# Revit family: Bath&ShoverMixer-Joystick-FloorMounted-Vitra-İstanbulSeries-A41819
name_source: partatom
category: Plumbing Fixtures
revit_build: Autodesk Revit 2017 (Build: 20160225_1515(x64)
units: mm (PartAtom-declared; Revit-internal decimal feet)

## family parameters
Cut with Voids When Loaded = No
Host = Face
OmniClass Number = 23.45.55.17
OmniClass Title = Mixing Faucets
Part Type = Normal
Room Calculation Point = No
Round Connector Dimension = Use Diameter
Shared = Yes

## types (7) — shared parameters
BIMobject category = Bath/Shower Mixer
Brand = Vitra
CW Connection = Yes
Description = Istanbul Joystick Bath/Shower Mixer
with Handshower-Floor Mounted
Design country = Turkey
HW Connection = Yes
Hot Water Supply (max.) = 80 °C
Hot Water temperature, factory set to = 38 °C
IFC Classification = Sanitary Terminal
Installation instructions = https://cdn.vitra.com.tr
Main Material = Brass
Manufacturer = Vitra
Manufacturer name = Vitra
Masterformat 2014 Code = 22 40 00
Masterformat 2014 Description = Plumbing Fixtures
Min. flow pressure of = 0.5 bar
Mounting type = FloorStanding
NBS Referans Code = 45-35-70/315
NBS Referans Description = Water supply fittings for baths
Nominal Depth (mm) = 315 mm  [stored 1.03346 ft]
Nominal Height (mm) = 920 mm
Nominal Width (mm) = 210 mm  [stored 0.688976 ft]
Number Of Connections = 2
OmniClass Code = 23.45.55.17
OmniClass Description = Mixing Faucets
Primary Material = <By Category>
Product Guid = https://cdn.vitra.com.tr
Product Properties = with Handshower-Floor Mounted
Product Type = Bath/Shower mixer
Product certification = https://www.vitraglobal.com
Product family = İstanbul
Product group = Bath/Shower mixer
Range of Hot Water Supply = 5 - 65 °C
Range of flow pressure = 1 - 5 bar
Test Pressure = 16 bar
URL = https://vitraglobal.com
Uniclass 1.4 Code = L725111
Uniclass 1.4 Description = Mixer taps
Uniclass 2.0 Code = Pr_40_20_87_09
Uniclass 2.0 Description = Bath taps
Uniclass 2015 Code = Pr_40_20_87_09
Uniclass 2015 Name = Bath taps
Uniformat II Code = 22 40 00
Uniformat II Description = Plumbing Fixture
Vent Connection = No
Waste Connection = No
Weight Net (kg) = 3.7
Youtube = https://www.youtube.com
zero-valued in all types: Default Elevation

## per-type parameters (varying)
| type | Article No. (default) | Coating Material | Color | Connection Diameter (mm) | Model | Product SKU | Product data url | Technical description | Warranty Period (Year) |
| Bath&ShoverMixer-Joystick-withHandshower-Vitra-İstanbulSeries-A4181923VUK | A4181923VUK | Gold | Gold | 15 mm  [stored 0.0492126 ft] | A4181923VUK | A4181923VUK | https://www.vitraglobal.com | https://www.vitraglobal.com | 7 Years |
| Bath&ShoverMixer-Joystick-withHandshower-Vitra-İstanbulSeries-A41819VUK | A41819VUK | Chrome | Chrome | 15 mm  [stored 0.0492126 ft] | A41819VUK | A41819VUK | https://www.vitraglobal.com | https://www.vitraglobal.com | 7 Years |
| Bath&ShoverMixer-Joystick-withHandshower-Vitra-İstanbulSeries-A41819IND | A41819IND | Chrome | Chrome | 15 mm  [stored 0.0492126 ft] | A41819IND | A41819IND | https://www.vitraglobal.com | https://www.vitraglobal.com | 7 Years |
| Bath&ShoverMixer-Joystick-withHandshower-Vitra-İstanbulSeries-A4181923 | A4181923 | Gold | Gold | 10 mm  [stored 0.0328084 ft] | A4181923 | A4181923 | https://www.vitra.com.tr | https://www.vitra.com.tr | 10 Years |
| Bath&ShoverMixer-Joystick-withHandshower-Vitra-İstanbulSeries-A4181923EXP | A4181923EXP | Gold | Gold | 10 mm  [stored 0.0328084 ft] | A4181923EXP | A4181923EXP | https://www.vitraglobal.com | https://www.vitraglobal.com | 7 Years |
| Bath&ShoverMixer-Joystick-withHandshower-Vitra-İstanbulSeries-A41819EXP | A41819EXP | Chrome | Chrome | 10 mm  [stored 0.0328084 ft] | A41819EXP | A41819EXP | https://www.vitraglobal.com | https://www.vitraglobal.com | 7 Years |
| Bath&ShoverMixer-Joystick-withHandshower-Vitra-İstanbulSeries-A41819 | A41819 | Chrome | Chrome | 10 mm  [stored 0.0328084 ft] | A41819 | A41819 | https://www.vitra.com.tr | https://www.vitra.com.tr | 10 Years |

note: [stored X ft] marks values corroborated as IEEE doubles in the binary element streams (Revit-internal decimal feet)

## geometry (parser evidence)
native form markers: Sweep x2
no freeform markers — native parametric forms only
